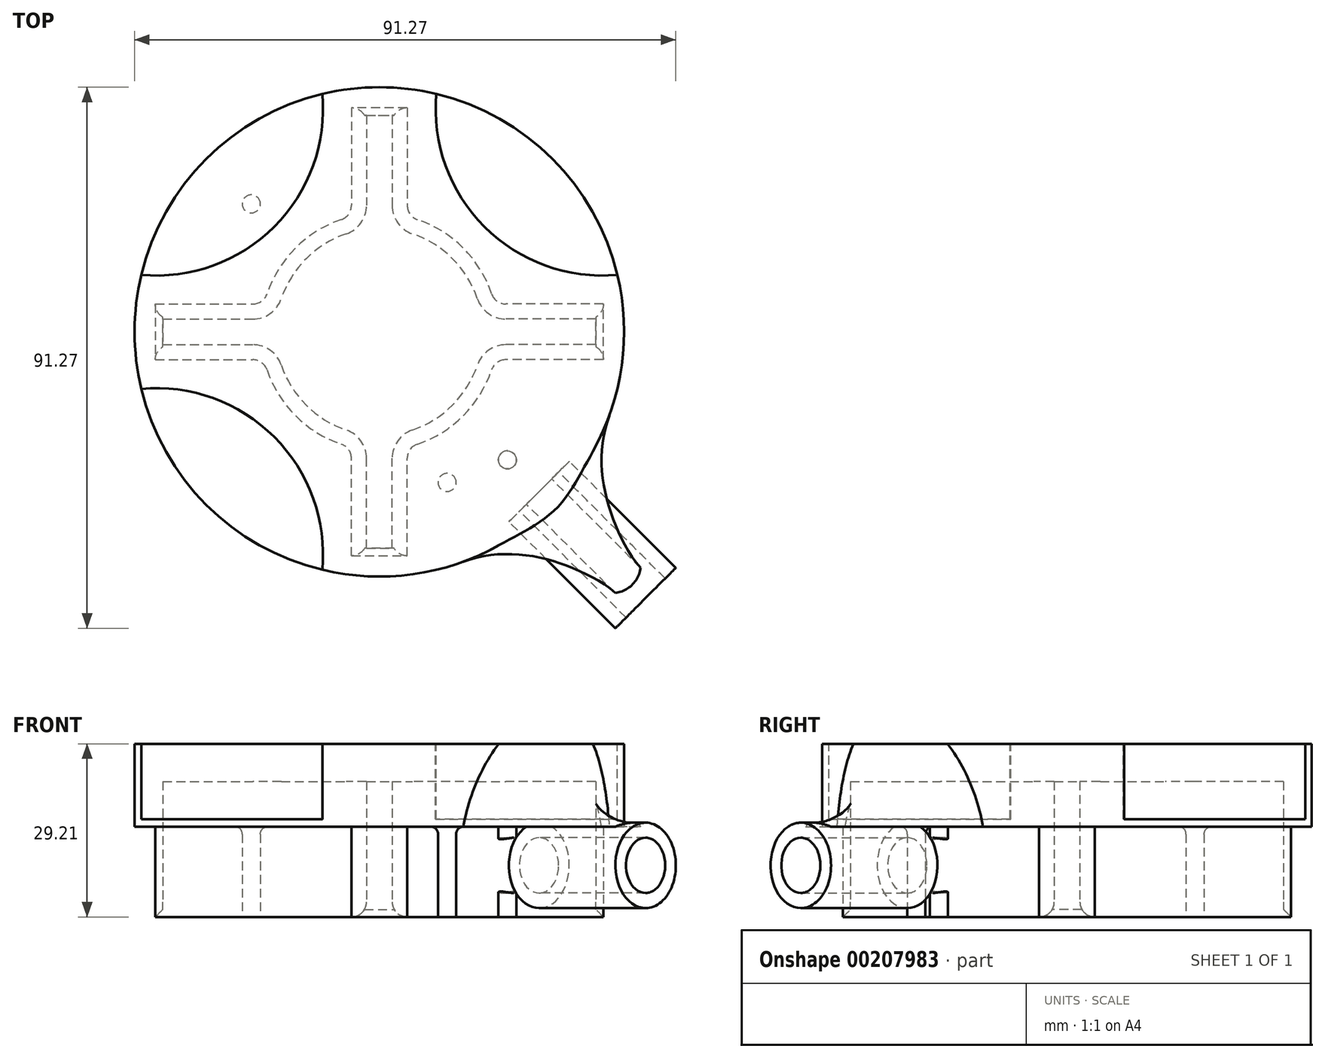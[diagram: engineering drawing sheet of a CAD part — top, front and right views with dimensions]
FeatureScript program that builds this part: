
annotation { "Feature Type Name" : "Feature", "Feature Type Description" : "" }
export const myFeature = defineFeature(function(context is Context, id is Id, definition is map)
    precondition{}
    {
        {
            var Q0;
            Q0=qCreatedBy(makeId("Top.planeOp"),FACE);
            var sketch = newSketch(context, id + "F0", { "sketchPlane" : qUnion([Q0])});
            skCircle(sketch, "E0", {"center": v(0, 0) * mm, "radius": 41.28 * mm});
            skCircle(sketch, "E1", {"center": v(0, 0) * mm, "radius": 17.46 * mm});
            skLineSegment(sketch, "E2", {"start": v(0, 0) * mm, "end": v(0, -36.51) * mm, "construction": true});
            skLineSegment(sketch, "E3", {"start": v(0, -36.51) * mm, "end": v(2.16, -36.51) * mm});
            skLineSegment(sketch, "E4", {"start": v(2.16, -36.51) * mm, "end": v(2.16, -17.33) * mm});
            skLineSegment(sketch, "E5.MirrorCS", {"start": v(-2.16, -36.51) * mm, "end": v(-2.16, -17.33) * mm});
            skLineSegment(sketch, "E6.MirrorCS", {"start": v(0, -36.51) * mm, "end": v(-2.16, -36.51) * mm});
            skLineSegment(sketch, "E7.1.0", {"start": v(36.51, -2.16) * mm, "end": v(17.33, -2.16) * mm});
            skLineSegment(sketch, "E7.1.1", {"start": v(36.51, 2.16) * mm, "end": v(17.33, 2.16) * mm});
            skLineSegment(sketch, "E7.1.2", {"start": v(36.51, 0) * mm, "end": v(36.51, 2.16) * mm});
            skLineSegment(sketch, "E7.1.3", {"start": v(36.51, 0) * mm, "end": v(36.51, -2.16) * mm});
            skLineSegment(sketch, "E7.2.0", {"start": v(2.16, 36.51) * mm, "end": v(2.16, 17.33) * mm});
            skLineSegment(sketch, "E7.2.1", {"start": v(-2.16, 36.51) * mm, "end": v(-2.16, 17.33) * mm});
            skLineSegment(sketch, "E7.2.2", {"start": v(0, 36.51) * mm, "end": v(-2.16, 36.51) * mm});
            skLineSegment(sketch, "E7.2.3", {"start": v(0, 36.51) * mm, "end": v(2.16, 36.51) * mm});
            skLineSegment(sketch, "E7.anchor1", {"start": v(0, 0) * mm, "end": v(-2.16, -36.51) * mm, "construction": true});
            skLineSegment(sketch, "E7.anchor2", {"start": v(0, 0) * mm, "end": v(2.16, 36.51) * mm, "construction": true});
            skLineSegment(sketch, "E8", {"start": v(0, 36.51) * mm, "end": v(0, -36.51) * mm, "construction": true});
            skLineSegment(sketch, "E9.MirrorCS", {"start": v(-36.51, -2.16) * mm, "end": v(-17.33, -2.16) * mm});
            skLineSegment(sketch, "E10.MirrorCS", {"start": v(-36.51, 0) * mm, "end": v(-36.51, -2.16) * mm});
            skLineSegment(sketch, "E11.MirrorCS", {"start": v(-36.51, 0) * mm, "end": v(-36.51, 2.16) * mm});
            skLineSegment(sketch, "E12.MirrorCS", {"start": v(-36.51, 2.16) * mm, "end": v(-17.33, 2.16) * mm});
            skLineSegment(sketch, "E13", {"start": v(0, 0) * mm, "end": v(55.78, -55.78) * mm, "construction": true});
            skLineSegment(sketch, "E14", {"start": v(55.78, -55.78) * mm, "end": v(36.51, -36.51) * mm, "construction": true});
            skLineSegment(sketch, "E15", {"start": v(55.78, -55.78) * mm, "end": v(60.27, -51.29) * mm});
            skLineSegment(sketch, "E16", {"start": v(60.27, -51.29) * mm, "end": v(33.33, -24.35) * mm});
            skLineSegment(sketch, "E17.MirrorCS", {"start": v(51.29, -60.27) * mm, "end": v(24.35, -33.33) * mm});
            skLineSegment(sketch, "E18.MirrorCS", {"start": v(55.78, -55.78) * mm, "end": v(51.29, -60.27) * mm});
            skSolve(sketch);
        }
        {
            var Q0;
            Q0=makeQuery(id+"F0.imprint","IMPRINT",FACE,{"disambiguationData":[TD([[makeQuery(id+"F0.imprint","IMPRINT",EDGE,{"derivedFrom":sQuery(id+"F0.wireOp",EDGE,"E0")}),1.0]])]});
            extrude(context, id + "F1", {"entities" : qUnion([Q0]), "depth" : 22.86 * mm});
        }
        {
            var Q0;
            Q0=makeQuery(id+"F1.opExtrude","CAP_FACE",FACE,{"disambiguationData":[OSD([sQuery(id+"F0.wireOp",EDGE,"E0"),sQuery(id+"F0.wireOp",EDGE,"E1"),sQuery(id+"F0.wireOp",EDGE,"E3"),sQuery(id+"F0.wireOp",EDGE,"E4"),sQuery(id+"F0.wireOp",EDGE,"E5.MirrorCS"),sQuery(id+"F0.wireOp",EDGE,"E6.MirrorCS"),sQuery(id+"F0.wireOp",EDGE,"E7.1.0"),sQuery(id+"F0.wireOp",EDGE,"E7.1.1"),sQuery(id+"F0.wireOp",EDGE,"E7.1.2"),sQuery(id+"F0.wireOp",EDGE,"E7.1.3"),sQuery(id+"F0.wireOp",EDGE,"E7.2.0"),sQuery(id+"F0.wireOp",EDGE,"E7.2.1"),sQuery(id+"F0.wireOp",EDGE,"E7.2.2"),sQuery(id+"F0.wireOp",EDGE,"E7.2.3"),sQuery(id+"F0.wireOp",EDGE,"E9.MirrorCS"),sQuery(id+"F0.wireOp",EDGE,"E10.MirrorCS"),sQuery(id+"F0.wireOp",EDGE,"E11.MirrorCS"),sQuery(id+"F0.wireOp",EDGE,"E12.MirrorCS")])],"isStart":false});
            var sketch = newSketch(context, id + "F2", { "sketchPlane" : qUnion([Q0])});
            skCircle(sketch, "E19", {"center": v(0, 0) * mm, "radius": 41.28 * mm});
            skSolve(sketch);
        }
        {
            var Q0;
            Q0 = qSketchRegion(id + "F2", true);
            extrude(context, id + "F3", {"entities" : qUnion([Q0]), "operationType" : NewBodyOperationType.ADD, "depth" : 6.35 * mm});
        }
        {
            var Q0;
            Q0=makeQuery(id+"F1.opExtrude","SWEPT_EDGE",EDGE,{"disambiguationData":[OSD([sQuery(id+"F0.wireOp",EDGE,"E1"),sQuery(id+"F0.wireOp",EDGE,"E4")])]});
            var Q1;
            Q1=makeQuery(id+"F1.opExtrude","SWEPT_EDGE",EDGE,{"disambiguationData":[OSD([sQuery(id+"F0.wireOp",EDGE,"E1"),sQuery(id+"F0.wireOp",EDGE,"E5.MirrorCS")])]});
            var Q2;
            Q2=makeQuery(id+"F1.opExtrude","SWEPT_EDGE",EDGE,{"disambiguationData":[OSD([sQuery(id+"F0.wireOp",EDGE,"E1"),sQuery(id+"F0.wireOp",EDGE,"E7.1.0")])]});
            var Q3;
            Q3=makeQuery(id+"F1.opExtrude","SWEPT_EDGE",EDGE,{"disambiguationData":[OSD([sQuery(id+"F0.wireOp",EDGE,"E1"),sQuery(id+"F0.wireOp",EDGE,"E7.1.1")])]});
            var Q4;
            Q4=makeQuery(id+"F1.opExtrude","SWEPT_EDGE",EDGE,{"disambiguationData":[OSD([sQuery(id+"F0.wireOp",EDGE,"E1"),sQuery(id+"F0.wireOp",EDGE,"E9.MirrorCS")])]});
            var Q5;
            Q5=makeQuery(id+"F1.opExtrude","SWEPT_EDGE",EDGE,{"disambiguationData":[OSD([sQuery(id+"F0.wireOp",EDGE,"E1"),sQuery(id+"F0.wireOp",EDGE,"E12.MirrorCS")])]});
            var Q6;
            Q6=makeQuery(id+"F1.opExtrude","SWEPT_EDGE",EDGE,{"disambiguationData":[OSD([sQuery(id+"F0.wireOp",EDGE,"E1"),sQuery(id+"F0.wireOp",EDGE,"E7.2.1")])]});
            var Q7;
            Q7=makeQuery(id+"F1.opExtrude","SWEPT_EDGE",EDGE,{"disambiguationData":[OSD([sQuery(id+"F0.wireOp",EDGE,"E1"),sQuery(id+"F0.wireOp",EDGE,"E7.2.0")])]});
            fillet(context, id + "F4", {"entities" : qUnion([Q0, Q1, Q2, Q3, Q4, Q5, Q6, Q7]), "radius" : 5.08 * mm, "tangentPropagation" : true, "allowEdgeOverflow" : false});
        }
        {
            var Q0;
            {var subQ0=sQuery(id+"F0.wireOp",EDGE,"E1");Q0=makeQuery(id+"F1.opExtrude","CAP_EDGE",EDGE,{"disambiguationData":[OSD([subQ0]),TDD([makeQuery(id+"F0.imprint","IMPRINT",EDGE,{"disambiguationData":[TD([[makeQuery(id+"F0.imprint","INTERSECT",VERTEX,{"derivedFrom":[subQ0,sQuery(id+"F0.wireOp",EDGE,"E5.MirrorCS")]}),1.0]])],"derivedFrom":subQ0})])],"isStart":true});}
            var Q1;
            {var subQ0=sQuery(id+"F0.wireOp",EDGE,"E1");Q1=makeQuery(id+"F1.opExtrude","CAP_EDGE",EDGE,{"disambiguationData":[OSD([subQ0]),TDD([makeQuery(id+"F0.imprint","IMPRINT",EDGE,{"disambiguationData":[TD([[makeQuery(id+"F0.imprint","INTERSECT",VERTEX,{"derivedFrom":[subQ0,sQuery(id+"F0.wireOp",EDGE,"E4")]}),-1.0]])],"derivedFrom":subQ0})])],"isStart":true});}
            var Q2;
            {var subQ0=sQuery(id+"F0.wireOp",EDGE,"E1");Q2=makeQuery(id+"F1.opExtrude","CAP_EDGE",EDGE,{"disambiguationData":[OSD([subQ0]),TDD([makeQuery(id+"F0.imprint","IMPRINT",EDGE,{"disambiguationData":[TD([[makeQuery(id+"F0.imprint","INTERSECT",VERTEX,{"derivedFrom":[subQ0,sQuery(id+"F0.wireOp",EDGE,"E7.1.1")]}),-1.0]])],"derivedFrom":subQ0})])],"isStart":true});}
            var Q3;
            {var subQ0=sQuery(id+"F0.wireOp",EDGE,"E1");Q3=makeQuery(id+"F1.opExtrude","CAP_EDGE",EDGE,{"disambiguationData":[OSD([subQ0]),TDD([makeQuery(id+"F0.imprint","IMPRINT",EDGE,{"disambiguationData":[TD([[makeQuery(id+"F0.imprint","INTERSECT",VERTEX,{"derivedFrom":[subQ0,sQuery(id+"F0.wireOp",EDGE,"E7.2.1")]}),-1.0]])],"derivedFrom":subQ0})])],"isStart":true});}
            fillet(context, id + "F5", {"entities" : qUnion([Q0, Q1, Q2, Q3]), "radius" : 2.54 * mm, "tangentPropagation" : true, "allowEdgeOverflow" : false});
        }
        {
            var Q0;
            Q0=makeQuery(id+"F1.opExtrude","CAP_EDGE",EDGE,{"disambiguationData":[OSD([sQuery(id+"F0.wireOp",EDGE,"E10.MirrorCS"),sQuery(id+"F0.wireOp",EDGE,"E11.MirrorCS")])],"isStart":true});
            var Q1;
            Q1=makeQuery(id+"F1.opExtrude","CAP_EDGE",EDGE,{"disambiguationData":[OSD([sQuery(id+"F0.wireOp",EDGE,"E3"),sQuery(id+"F0.wireOp",EDGE,"E6.MirrorCS")])],"isStart":true});
            var Q2;
            Q2=makeQuery(id+"F1.opExtrude","CAP_EDGE",EDGE,{"disambiguationData":[OSD([sQuery(id+"F0.wireOp",EDGE,"E7.1.2"),sQuery(id+"F0.wireOp",EDGE,"E7.1.3")])],"isStart":true});
            var Q3;
            Q3=makeQuery(id+"F1.opExtrude","CAP_EDGE",EDGE,{"disambiguationData":[OSD([sQuery(id+"F0.wireOp",EDGE,"E7.2.2"),sQuery(id+"F0.wireOp",EDGE,"E7.2.3")])],"isStart":true});
            chamfer(context, id + "F6", {"entities" : qUnion([Q0, Q1, Q2, Q3]), "width" : 1.27 * mm, "tangentPropagation" : true});
        }
        {
            var Q0;
            Q0=makeQuery(id+"F3.opExtrude","CAP_FACE",FACE,{"disambiguationData":[OSD([sQuery(id+"F2.wireOp",EDGE,"E19")])],"isStart":false});
            var sketch = newSketch(context, id + "F7", { "sketchPlane" : qUnion([Q0])});
            skLineSegment(sketch, "E20", {"start": v(0, 41.28) * mm, "end": v(0, -41.28) * mm, "construction": true});
            skLineSegment(sketch, "E21", {"start": v(-41.28, 0) * mm, "end": v(41.28, 0) * mm, "construction": true});
            skLineSegment(sketch, "E22", {"start": v(0, 0) * mm, "end": v(-45.75, 45.75) * mm, "construction": true});
            skArc(sketch, "E23", {"start": v(-40.14, 9.6) * mm, "mid": v(-17.73, 17.73) * mm, "end": v(-9.6, 40.14) * mm});
            skCircle(sketch, "E24.0", {"center": v(0, 0) * mm, "radius": 41.28 * mm});
            skArc(sketch, "E25.1.0", {"start": v(-9.6, -40.14) * mm, "mid": v(-17.73, -17.73) * mm, "end": v(-40.14, -9.6) * mm});
            skArc(sketch, "E25.3.0", {"start": v(9.6, 40.14) * mm, "mid": v(17.73, 17.73) * mm, "end": v(40.14, 9.6) * mm});
            skSolve(sketch);
        }
        {
            var Q0;
            {var subQ0=sQuery(id+"F7.wireOp",EDGE,"E25.2.0");Q0=makeQuery(id+"F7.imprint","IMPRINT",FACE,{"disambiguationData":[TD([[makeQuery(id+"F7.imprint","IMPRINT",EDGE,{"derivedFrom":subQ0}),1.0]])]});}
            var Q1;
            {var subQ0=sQuery(id+"F7.wireOp",EDGE,"E25.1.0");Q1=makeQuery(id+"F7.imprint","IMPRINT",FACE,{"disambiguationData":[TD([[makeQuery(id+"F7.imprint","IMPRINT",EDGE,{"derivedFrom":subQ0}),1.0]])]});}
            var Q2;
            {var subQ0=sQuery(id+"F7.wireOp",EDGE,"E25.3.0");Q2=makeQuery(id+"F7.imprint","IMPRINT",FACE,{"disambiguationData":[TD([[makeQuery(id+"F7.imprint","IMPRINT",EDGE,{"derivedFrom":subQ0}),1.0]])]});}
            var Q3;
            {var subQ0=sQuery(id+"F7.wireOp",EDGE,"E23");Q3=makeQuery(id+"F7.imprint","IMPRINT",FACE,{"disambiguationData":[TD([[makeQuery(id+"F7.imprint","IMPRINT",EDGE,{"derivedFrom":subQ0}),1.0]])]});}
            extrude(context, id + "F8", {"entities" : qUnion([Q0, Q1, Q2, Q3]), "operationType" : NewBodyOperationType.REMOVE, "oppositeDirection" : true, "depth" : 12.7 * mm});
        }
        {
            var Q0;
            Q0=makeQuery(id+"F1.opExtrude","CAP_FACE",FACE,{"disambiguationData":[OSD([sQuery(id+"F0.wireOp",EDGE,"E0"),sQuery(id+"F0.wireOp",EDGE,"E1"),sQuery(id+"F0.wireOp",EDGE,"E3"),sQuery(id+"F0.wireOp",EDGE,"E4"),sQuery(id+"F0.wireOp",EDGE,"E5.MirrorCS"),sQuery(id+"F0.wireOp",EDGE,"E6.MirrorCS"),sQuery(id+"F0.wireOp",EDGE,"E7.1.0"),sQuery(id+"F0.wireOp",EDGE,"E7.1.1"),sQuery(id+"F0.wireOp",EDGE,"E7.1.2"),sQuery(id+"F0.wireOp",EDGE,"E7.1.3"),sQuery(id+"F0.wireOp",EDGE,"E7.2.0"),sQuery(id+"F0.wireOp",EDGE,"E7.2.1"),sQuery(id+"F0.wireOp",EDGE,"E7.2.2"),sQuery(id+"F0.wireOp",EDGE,"E7.2.3"),sQuery(id+"F0.wireOp",EDGE,"E9.MirrorCS"),sQuery(id+"F0.wireOp",EDGE,"E10.MirrorCS"),sQuery(id+"F0.wireOp",EDGE,"E11.MirrorCS"),sQuery(id+"F0.wireOp",EDGE,"E12.MirrorCS")])],"isStart":true});
            var sketch = newSketch(context, id + "F9", { "sketchPlane" : qUnion([Q0])});
            skLineSegment(sketch, "E26", {"start": v(0, 41.28) * mm, "end": v(0, 0) * mm, "construction": true});
            skLineSegment(sketch, "E27", {"start": v(0, 0) * mm, "end": v(-41.28, 0) * mm, "construction": true});
            skLineSegment(sketch, "E28", {"start": v(-21.59, 0) * mm, "end": v(-21.59, 21.59) * mm, "construction": true});
            skLineSegment(sketch, "E29", {"start": v(-21.59, 21.59) * mm, "end": v(0, 21.6) * mm, "construction": true});
            skCircle(sketch, "E30", {"center": v(-21.59, 21.59) * mm, "radius": 1.52 * mm});
            skCircle(sketch, "E31.MirrorC", {"center": v(21.59, 21.59) * mm, "radius": 1.52 * mm});
            skCircle(sketch, "E32.MirrorC", {"center": v(-21.59, -21.59) * mm, "radius": 1.52 * mm});
            skCircle(sketch, "E33.MirrorC", {"center": v(21.59, -21.59) * mm, "radius": 1.52 * mm});
            skLineSegment(sketch, "E34", {"start": v(11.43, 0) * mm, "end": v(11.43, 25.4) * mm, "construction": true});
            skLineSegment(sketch, "E35", {"start": v(11.43, 25.4) * mm, "end": v(0, 25.4) * mm, "construction": true});
            skCircle(sketch, "E36", {"center": v(11.43, 25.4) * mm, "radius": 1.52 * mm});
            skSolve(sketch);
        }
        {
            var Q0;
            Q0=makeQuery(id+"F9.imprint","IMPRINT",FACE,{"disambiguationData":[TD([[makeQuery(id+"F9.imprint","IMPRINT",EDGE,{"derivedFrom":sQuery(id+"F9.wireOp",EDGE,"E30")}),1.0]])]});
            var Q1;
            Q1=makeQuery(id+"F9.imprint","IMPRINT",FACE,{"disambiguationData":[TD([[makeQuery(id+"F9.imprint","IMPRINT",EDGE,{"derivedFrom":sQuery(id+"F9.wireOp",EDGE,"E33.MirrorC")}),1.0]])]});
            var Q2;
            Q2=makeQuery(id+"F9.imprint","IMPRINT",FACE,{"disambiguationData":[TD([[makeQuery(id+"F9.imprint","IMPRINT",EDGE,{"derivedFrom":sQuery(id+"F9.wireOp",EDGE,"E32.MirrorC")}),-1.0]])]});
            var Q3;
            Q3=makeQuery(id+"F9.imprint","IMPRINT",FACE,{"disambiguationData":[TD([[makeQuery(id+"F9.imprint","IMPRINT",EDGE,{"derivedFrom":sQuery(id+"F9.wireOp",EDGE,"E31.MirrorC")}),-1.0]])]});
            extrude(context, id + "F10", {"entities" : qUnion([Q0, Q1, Q2, Q3]), "operationType" : NewBodyOperationType.REMOVE, "oppositeDirection" : true, "depth" : 15.24 * mm});
        }
        {
            var Q0;
            Q0=makeQuery(id+"F10.boolean.opBoolean","COPY",EDGE,{"derivedFrom":makeQuery(id+"F10.opExtrude","CAP_EDGE",EDGE,{"disambiguationData":[OSD([sQuery(id+"F9.wireOp",EDGE,"E30")])],"isStart":false})});
            var Q1;
            Q1=makeQuery(id+"F10.boolean.opBoolean","COPY",EDGE,{"derivedFrom":makeQuery(id+"F10.opExtrude","CAP_EDGE",EDGE,{"disambiguationData":[OSD([sQuery(id+"F9.wireOp",EDGE,"E36")])],"isStart":false})});
            var Q2;
            Q2=makeQuery(id+"F10.boolean.opBoolean","COPY",EDGE,{"derivedFrom":makeQuery(id+"F10.opExtrude","CAP_EDGE",EDGE,{"disambiguationData":[OSD([sQuery(id+"F9.wireOp",EDGE,"E33.MirrorC")])],"isStart":false})});
            var Q3;
            Q3=makeQuery(id+"F10.boolean.opBoolean","COPY",EDGE,{"derivedFrom":makeQuery(id+"F10.opExtrude","CAP_EDGE",EDGE,{"disambiguationData":[OSD([sQuery(id+"F9.wireOp",EDGE,"E32.MirrorC")])],"isStart":false})});
            fillet(context, id + "F11", {"entities" : qUnion([Q0, Q1, Q2, Q3]), "radius" : 1.27 * mm, "tangentPropagation" : true, "allowEdgeOverflow" : false});
        }
        {
            var Q0;
            Q0=qCreatedBy(makeId("Front.planeOp"),FACE);
            var Q1;
            Q1=qCreatedBy(makeId("Right.planeOp"),FACE);
            cPlane(context, id + "F12", {"entities" : qUnion([Q0, Q1]), "cplaneType" : CPlaneType.MID_PLANE, "offset" : 25.4 * mm, "flipAlignment" : true, "width" : 152.4 * mm, "height" : 152.4 * mm});
        }
        {
            var Q0;
            Q0=qCreatedBy(id+"F12.planeOp",FACE);
            cPlane(context, id + "F13", {"entities" : qUnion([Q0]), "cplaneType" : CPlaneType.OFFSET, "offset" : 38.1 * mm, "width" : 152.4 * mm, "height" : 152.4 * mm});
        }
        {
            var Q0;
            Q0=qCreatedBy(id+"F13.planeOp",FACE);
            var sketch = newSketch(context, id + "F14", { "sketchPlane" : qUnion([Q0])});
            skLineSegment(sketch, "E37.0", {"start": v(-35.18, 29.21) * mm, "end": v(35.18, 29.21) * mm});
            skLineSegment(sketch, "E38.0", {"start": v(-41.28, 0) * mm, "end": v(41.28, 0) * mm});
            skLineSegment(sketch, "E39", {"start": v(0, 29.21) * mm, "end": v(0, 0) * mm, "construction": true});
            skCircle(sketch, "E40", {"center": v(0, 8.7) * mm, "radius": 4.66 * mm});
            skSolve(sketch);
        }
        {
            var Q0;
            Q0 = qSketchRegion(id + "F14", true);
            extrude(context, id + "F15", {"entities" : qUnion([Q0]), "operationType" : NewBodyOperationType.REMOVE, "oppositeDirection" : true, "depth" : 16.76 * mm, "hasSecondDirection" : true, "secondDirectionOppositeDirection" : false, "secondDirectionDepth" : 25.4 * mm});
        }
        {
            var Q0;
            Q0=qCreatedBy(id+"F13.planeOp",FACE);
            var sketch = newSketch(context, id + "F16", { "sketchPlane" : qUnion([Q0])});
            skCircle(sketch, "E41.0", {"center": v(0, 8.7) * mm, "radius": 4.66 * mm});
            skCircle(sketch, "E42", {"center": v(0, 8.7) * mm, "radius": 7.2 * mm});
            skSolve(sketch);
        }
        {
            var Q0;
            Q0 = qSketchRegion(id + "F16", true);
            extrude(context, id + "F17", {"entities" : qUnion([Q0]), "operationType" : NewBodyOperationType.ADD, "depth" : 25.4 * mm});
        }
        {
            var Q0;
            Q0=makeQuery(id+"F17.boolean.opBoolean","INTERSECT",EDGE,{"derivedFrom":[makeQuery(id+"F3.boolean.opBoolean","MERGE",FACE,{"derivedFrom":[makeQuery(id+"F1.opExtrude","SWEPT_FACE",FACE,{"disambiguationData":[OSD([sQuery(id+"F0.wireOp",EDGE,"E0")])]}),makeQuery(id+"F3.opExtrude","SWEPT_FACE",FACE,{"disambiguationData":[OSD([sQuery(id+"F2.wireOp",EDGE,"E19")])]})]}),makeQuery(id+"F17.opExtrude","SWEPT_FACE",FACE,{"disambiguationData":[OSD([sQuery(id+"F16.wireOp",EDGE,"E42")])]})]});
            fillet(context, id + "F18", {"entities" : qUnion([Q0]), "radius" : 19.05 * mm, "tangentPropagation" : true, "allowEdgeOverflow" : false});
        }
    });
